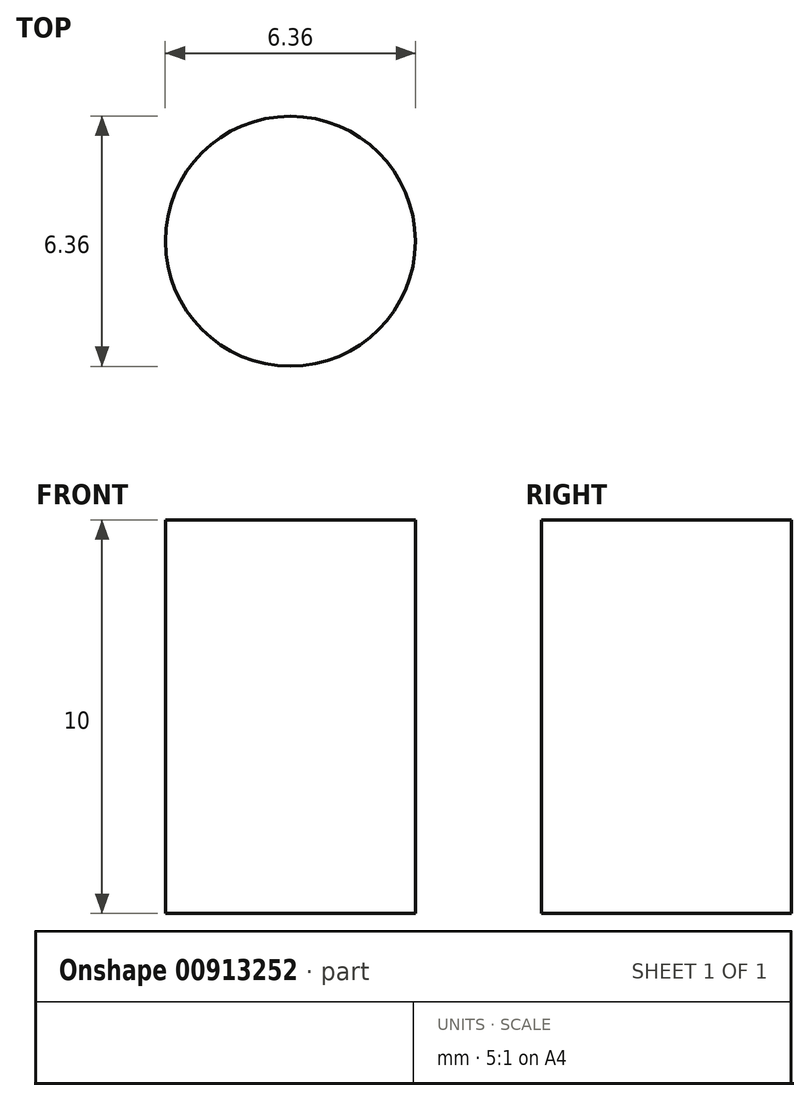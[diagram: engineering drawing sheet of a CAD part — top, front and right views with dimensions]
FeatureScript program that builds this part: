
annotation { "Feature Type Name" : "Feature", "Feature Type Description" : "" }
export const myFeature = defineFeature(function(context is Context, id is Id, definition is map)
    precondition{}
    {
        {
            var Q0;
            Q0=qCreatedBy(makeId("Front.planeOp"),FACE);
            var sketch = newSketch(context, id + "F0", { "sketchPlane" : qUnion([Q0])});
            skLineSegment(sketch, "E0.bottom", {"start": v(0, 0) * mm, "end": v(-3.17, 0) * mm});
            skLineSegment(sketch, "E0.top", {"start": v(0, 10) * mm, "end": v(-3.18, 10) * mm});
            skLineSegment(sketch, "E0.left", {"start": v(0, 0) * mm, "end": v(0, 10) * mm});
            skLineSegment(sketch, "E0.right", {"start": v(-3.18, 0) * mm, "end": v(-3.18, 10) * mm});
            skSolve(sketch);
        }
        {
            var Q0;
            Q0=makeQuery(id+"F0.imprint","IMPRINT",FACE,{"disambiguationData":[TD([[makeQuery(id+"F0.imprint","IMPRINT",EDGE,{"derivedFrom":sQuery(id+"F0.wireOp",EDGE,"E0.bottom")}),-1.0]])]});
            var Q1;
            Q1=sQuery(id+"F0.wireOp",EDGE,"E0.left");
            revolve(context, id + "F1", {"surfaceOperationType" : NewSurfaceOperationType.NEW, "entities" : qUnion([Q0]), "axis" : qUnion([Q1]), "revolveType" : RevolveType.FULL});
        }
    });
